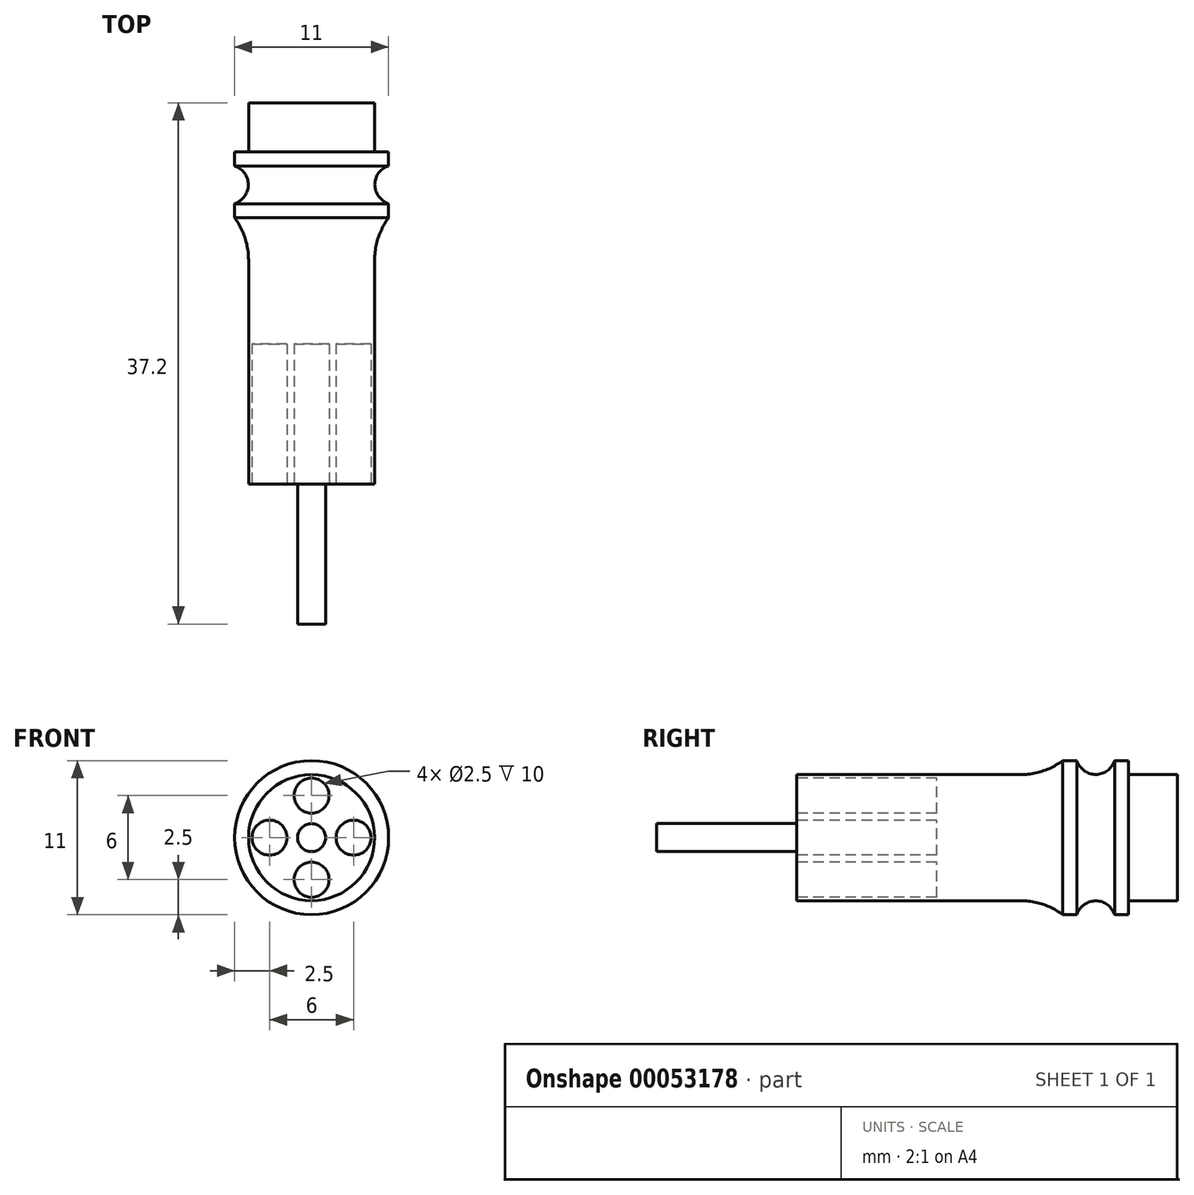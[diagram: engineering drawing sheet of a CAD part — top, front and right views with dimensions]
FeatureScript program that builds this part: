
annotation { "Feature Type Name" : "Feature", "Feature Type Description" : "" }
export const myFeature = defineFeature(function(context is Context, id is Id, definition is map)
    precondition{}
    {
        {
            var Q0;
            Q0=qCreatedBy(makeId("Front.planeOp"),FACE);
            var sketch = newSketch(context, id + "F0", { "sketchPlane" : qUnion([Q0])});
            skCircle(sketch, "E0", {"center": v(0, 0) * mm, "radius": 4.5 * mm});
            skSolve(sketch);
        }
        {
            var Q0;
            Q0 = qSketchRegion(id + "F0", true);
            extrude(context, id + "F1", {"entities" : qUnion([Q0]), "depth" : 19 * mm});
        }
        {
            var Q0;
            Q0 = qSketchRegion(id + "F0", true);
            extrude(context, id + "F2", {"entities" : qUnion([Q0]), "operationType" : NewBodyOperationType.ADD, "oppositeDirection" : true, "depth" : 4.7 * mm});
        }
        {
            var Q0;
            Q0=qCreatedBy(makeId("Front.planeOp"),FACE);
            var sketch = newSketch(context, id + "F3", { "sketchPlane" : qUnion([Q0])});
            skCircle(sketch, "E1", {"center": v(0, 0) * mm, "radius": 5.5 * mm});
            skSolve(sketch);
        }
        {
            var Q0;
            Q0=makeQuery(id+"F3.imprint","IMPRINT",FACE,{"disambiguationData":[TD([[makeQuery(id+"F3.imprint","IMPRINT",EDGE,{"derivedFrom":sQuery(id+"F3.wireOp",EDGE,"E1")}),1.0]])]});
            extrude(context, id + "F4", {"entities" : qUnion([Q0]), "operationType" : NewBodyOperationType.ADD, "oppositeDirection" : true, "depth" : 1 * mm});
        }
        {
            var Q0;
            {var subQ0=sQuery(id+"F0.wireOp",EDGE,"E0");Q0=makeQuery(id+"F4.boolean.opBoolean","INTERSECT",EDGE,{"derivedFrom":[makeQuery(id+"F2.boolean.opBoolean","MERGE",FACE,{"derivedFrom":[makeQuery(id+"F1.opExtrude","SWEPT_FACE",FACE,{"disambiguationData":[OSD([subQ0])]}),makeQuery(id+"F2.opExtrude","SWEPT_FACE",FACE,{"disambiguationData":[OSD([subQ0])]})]}),makeQuery(id+"F4.opExtrude","CAP_FACE",FACE,{"disambiguationData":[OSD([sQuery(id+"F3.wireOp",EDGE,"E1")])],"isStart":false})]});}
            fillet(context, id + "F5", {"entities" : qUnion([Q0]), "radius" : 1.5 * mm, "tangentPropagation" : true, "allowEdgeOverflow" : false});
        }
        {
            var Q0;
            {var subQ0=sQuery(id+"F0.wireOp",EDGE,"E0");Q0=makeQuery(id+"F4.boolean.opBoolean","INTERSECT",EDGE,{"derivedFrom":[makeQuery(id+"F2.boolean.opBoolean","MERGE",FACE,{"derivedFrom":[makeQuery(id+"F1.opExtrude","SWEPT_FACE",FACE,{"disambiguationData":[OSD([subQ0])]}),makeQuery(id+"F2.opExtrude","SWEPT_FACE",FACE,{"disambiguationData":[OSD([subQ0])]})]}),makeQuery(id+"F4.opExtrude","CAP_FACE",FACE,{"disambiguationData":[OSD([sQuery(id+"F3.wireOp",EDGE,"E1")])],"isStart":true})]});}
            fillet(context, id + "F6", {"entities" : qUnion([Q0]), "radius" : 5 * mm, "tangentPropagation" : true, "allowEdgeOverflow" : false});
        }
        {
            var Q0;
            Q0=makeQuery(id+"F1.opExtrude","CAP_FACE",FACE,{"disambiguationData":[OSD([sQuery(id+"F0.wireOp",EDGE,"E0")])],"isStart":false});
            var sketch = newSketch(context, id + "F7", { "sketchPlane" : qUnion([Q0])});
            skCircle(sketch, "E2", {"center": v(0, 0) * mm, "radius": 1 * mm});
            skSolve(sketch);
        }
        {
            var Q0;
            Q0=makeQuery(id+"F7.imprint","IMPRINT",FACE,{"disambiguationData":[TD([[makeQuery(id+"F7.imprint","IMPRINT",EDGE,{"derivedFrom":sQuery(id+"F7.wireOp",EDGE,"E2")}),1.0]])]});
            extrude(context, id + "F8", {"entities" : qUnion([Q0]), "operationType" : NewBodyOperationType.ADD, "depth" : 10 * mm});
        }
        {
            var Q0;
            Q0=makeQuery(id+"F1.opExtrude","CAP_FACE",FACE,{"disambiguationData":[OSD([sQuery(id+"F0.wireOp",EDGE,"E0")])],"isStart":false});
            var sketch = newSketch(context, id + "F9", { "sketchPlane" : qUnion([Q0])});
            skCircle(sketch, "E3", {"center": v(0, -3) * mm, "radius": 1.25 * mm});
            skCircle(sketch, "E4", {"center": v(0, 3) * mm, "radius": 1.25 * mm});
            skCircle(sketch, "E5", {"center": v(3, 0) * mm, "radius": 1.25 * mm});
            skCircle(sketch, "E6", {"center": v(-3, 0) * mm, "radius": 1.25 * mm});
            skSolve(sketch);
        }
        {
            var Q0;
            Q0 = qSketchRegion(id + "F9", true);
            extrude(context, id + "F10", {"entities" : qUnion([Q0]), "operationType" : NewBodyOperationType.REMOVE, "oppositeDirection" : true, "depth" : 10 * mm});
        }
        {
            var Q0;
            Q0=makeQuery(id+"F2.opExtrude","CAP_FACE",FACE,{"disambiguationData":[OSD([sQuery(id+"F0.wireOp",EDGE,"E0")])],"isStart":false});
            var sketch = newSketch(context, id + "F11", { "sketchPlane" : qUnion([Q0])});
            skCircle(sketch, "E7", {"center": v(0, 0) * mm, "radius": 4.5 * mm});
            skSolve(sketch);
        }
        {
            var Q0;
            Q0=makeQuery(id+"F11.imprint","IMPRINT",FACE,{"disambiguationData":[TD([[makeQuery(id+"F11.imprint","IMPRINT",EDGE,{"derivedFrom":sQuery(id+"F11.wireOp",EDGE,"E7")}),-1.0]])]});
            var sketch = newSketch(context, id + "F12", { "sketchPlane" : qUnion([Q0])});
            skCircle(sketch, "E8", {"center": v(0, 0) * mm, "radius": 5.5 * mm});
            skSolve(sketch);
        }
        {
            var Q0;
            Q0=makeQuery(id+"F11.imprint","IMPRINT",FACE,{"disambiguationData":[TD([[makeQuery(id+"F11.imprint","IMPRINT",EDGE,{"derivedFrom":sQuery(id+"F11.wireOp",EDGE,"E7")}),-1.0]])]});
            extrude(context, id + "F13", {"entities" : qUnion([Q0]), "operationType" : NewBodyOperationType.ADD, "depth" : 3.5 * mm});
        }
        {
            var Q0;
            Q0=makeQuery(id+"F12.imprint","IMPRINT",FACE,{"disambiguationData":[TD([[makeQuery(id+"F12.imprint","IMPRINT",EDGE,{"derivedFrom":sQuery(id+"F12.wireOp",EDGE,"E8")}),1.0]])]});
            extrude(context, id + "F14", {"entities" : qUnion([Q0]), "operationType" : NewBodyOperationType.ADD, "oppositeDirection" : true, "depth" : 1 * mm});
        }
        {
            var Q0;
            Q0=makeQuery(id+"F14.opExtrude","CAP_EDGE",EDGE,{"disambiguationData":[OSD([sQuery(id+"F11.wireOp",EDGE,"E7")])],"isStart":false});
            fillet(context, id + "F15", {"entities" : qUnion([Q0]), "radius" : 1.4 * mm, "tangentPropagation" : true, "allowEdgeOverflow" : false});
        }
    });
